# Revit family: TESK_Насос вертикальный_SVM(T)-32
name_source: partatom
category: Оборудование
units: mm (PartAtom-declared; Revit-internal decimal feet)

## family parameters
Всегда вертикально = Да
Классификация = Насос
На основе рабочей плоскости = Нет
Общий = Нет
При загрузке вырезать с полостями = Нет
Размер круглого соединителя = Использовать диаметр
Тип детали = Вставляется
Точка расчета площади = Нет

## types (64) — shared parameters
ADSK_Версия Revit = 2019
ADSK_Версия семейства = 1.0
ADSK_Диаметр условный = 65 мм
ADSK_Единица измерения = шт.
ADSK_Завод-изготовитель = TESK
ADSK_Классификация нагрузок = Прочее
ADSK_Количество = 1
ADSK_Количество фаз = 3
ADSK_Количество фаз числовое = 3
ADSK_Коэффициент мощности = 1
ADSK_Наименование краткое = Вертикальный многоступенчатый центробежный насос
ADSK_Напряжение = 400 В
URL = www.teskpump.ru
Материал_1 = TESK_Черный_Условный
Материал_2 = TESK_Нержавеющая сталь
Материал_КорпусДвигателя = TESK_Черный_Ребра_Условный
Таблица_Поиска = TESK_SVM(T)-32
УГО_Длина = 320 мм
Фланец_Толщина = 24 мм

## per-type parameters (varying)
| type | ADSK_Код изделия | ADSK_Масса | ADSK_Масса_Текст | ADSK_Наименование | ADSK_Номинальная мощность | ADSK_Полная мощность | D_Башня | Высота_Башня | Высота_Корпуса | Двигатель_Высота | Двигатель_ОтступКоробки | Двигатель_Ширина | Материал_КорпусУлитка | Напор максимальный | Толщина_ФланцаДвигателя |
| SVM 32-10-1 1.5kW 3x380V 50Hz IE3 | 7732-10-10003380NSSF | 67 | 67 | Вертикальный многоступенчатый центробежный насос SVM, DN65, PN25-40, Hmax=14м (3x380V 50Hz IE3) | 2 кВт | 2 кВ·А | 143 мм | 180 мм | 505 мм | 333 мм | 155 мм | 190 мм | TESK_Нержавеющая сталь | 14 | 10 мм |
| SVM 32-1 2.2kW 3x380V 50Hz IE3 | 7732-10003380NSSF | 67 | 67 | Вертикальный многоступенчатый центробежный насос SVM, DN65, PN25-40, Hmax=18м (3x380V 50Hz IE3) | 2 кВт | 2 кВ·А | 143 мм | 180 мм | 505 мм | 333 мм | 155 мм | 190 мм | TESK_Нержавеющая сталь | 18 | 10 мм |
| SVM 32-20-2 3kW 3x380V 50Hz IE3 | 7732-2-20003380NSSF | 83 | 83 | Вертикальный многоступенчатый центробежный насос SVM, DN65, PN25-40, Hmax=29м (3x380V 50Hz IE3) | 3 кВт | 3 кВ·А | 173 мм | 200 мм | 575 мм | 370 мм | 185 мм | 230 мм | TESK_Нержавеющая сталь | 29 | 11 мм |
| SVM 32-2 4kW 3x380V 50Hz IE3 | 7732-20003380NSSF | 83 | 83 | Вертикальный многоступенчатый центробежный насос SVM, DN65, PN25-40, Hmax=36м (3x380V 50Hz IE3) | 4 кВт | 4 кВ·А | 173 мм | 200 мм | 575 мм | 370 мм | 185 мм | 230 мм | TESK_Нержавеющая сталь | 36 | 11 мм |
| SVM 32-30-2 5.5kW 3x380V 50Hz IE3 | 7732-32003380NSSF | 100 | 100 | Вертикальный многоступенчатый центробежный насос SVM, DN65, PN25-40, Hmax=47м (3x380V 50Hz IE3) | 6 кВт | 6 кВ·А | 195 мм | 220 мм | 645 мм | 435 мм | 208 мм | 260 мм | TESK_Нержавеющая сталь | 47 | 13 мм |
| SVM 32-3 5.5kW 3x380V 50Hz IE3 | 7732-30003380NSSF | 100 | 100 | Вертикальный многоступенчатый центробежный насос SVM, DN65, PN25-40, Hmax=54м (3x380V 50Hz IE3) | 6 кВт | 6 кВ·А | 195 мм | 220 мм | 645 мм | 435 мм | 208 мм | 260 мм | TESK_Нержавеющая сталь | 54 | 13 мм |
| SVM 32-40-2 7.5kW 3x380V 50Hz IE3 | 7732-40-2003380NSSF | 109 | 109 | Вертикальный многоступенчатый центробежный насос SVM, DN65, PN25-40, Hmax=65м (3x380V 50Hz IE3) | 8 кВт | 8 кВ·А | 195 мм | 240 мм | 715 мм | 435 мм | 208 мм | 260 мм | TESK_Нержавеющая сталь | 65 | 13 мм |
| SVM 32-4 7.5kW 3x380V 50Hz IE3 | 7732-40003380NSSF | 109 | 109 | Вертикальный многоступенчатый центробежный насос SVM, DN65, PN25-40, Hmax=72м (3x380V 50Hz IE3) | 8 кВт | 8 кВ·А | 195 мм | 240 мм | 715 мм | 435 мм | 208 мм | 260 мм | TESK_Нержавеющая сталь | 72 | 13 мм |
| SVM 32-50-2 11kW 3x380V 50Hz IE3 | 7732-5-20003380NSSF | 181 | 181 | Вертикальный многоступенчатый центробежный насос SVM, DN65, PN25-40, Hmax=83м (3x380V 50Hz IE3) | 11 кВт | 11 кВ·А | 263 мм | 260 мм | 890 мм | 580 мм | 260 мм | 350 мм | TESK_Нержавеющая сталь | 83 | 17 мм |
| SVM 32-5 11kW 3x380V 50Hz IE3 | 7732-50003380NSSF | 181 | 181 | Вертикальный многоступенчатый центробежный насос SVM, DN65, PN25-40, Hmax=90м (3x380V 50Hz IE3) | 11 кВт | 11 кВ·А | 263 мм | 260 мм | 890 мм | 580 мм | 260 мм | 350 мм | TESK_Нержавеющая сталь | 90 | 17 мм |
| SVM 32-60-2 11kW 3x380V 50Hz IE3 | 7732-6-20003380NSSF | 185 | 185 | Вертикальный многоступенчатый центробежный насос SVM, DN65, PN25-40, Hmax=101м (3x380V 50Hz IE3) | 11 кВт | 11 кВ·А | 263 мм | 280 мм | 960 мм | 580 мм | 260 мм | 350 мм | TESK_Нержавеющая сталь | 101 | 17 мм |
| SVM 32-6 11kW 3x380V 50Hz IE3 | 7732-60003380NSSF | 185 | 185 | Вертикальный многоступенчатый центробежный насос SVM, DN65, PN25-40, Hmax=108м (3x380V 50Hz IE3) | 11 кВт | 11 кВ·А | 263 мм | 280 мм | 960 мм | 580 мм | 260 мм | 350 мм | TESK_Нержавеющая сталь | 108 | 17 мм |
| SVM 32-70-2 15kW 3x380V 50Hz IE3 | 7732-7-20003380NSSF | 199 | 199 | Вертикальный многоступенчатый центробежный насос SVM, DN65, PN25-40, Hmax=119м (3x380V 50Hz IE3) | 15 кВт | 15 кВ·А | 263 мм | 300 мм | 1030 мм | 580 мм | 260 мм | 350 мм | TESK_Нержавеющая сталь | 119 | 17 мм |
| SVM 32-7 15kW 3x380V 50Hz IE3 | 7732-70003380NSSF | 199 | 199 | Вертикальный многоступенчатый центробежный насос SVM, DN65, PN25-40, Hmax=126м (3x380V 50Hz IE3) | 15 кВт | 15 кВ·А | 263 мм | 300 мм | 1030 мм | 580 мм | 260 мм | 350 мм | TESK_Нержавеющая сталь | 126 | 17 мм |
| SVM 32-80-2 15kW 3x380V 50Hz IE3 | 7732-8-20003380NSSF | 203 | 203 | Вертикальный многоступенчатый центробежный насос SVM, DN65, PN25-40, Hmax=136м (3x380V 50Hz IE3) | 15 кВт | 15 кВ·А | 263 мм | 320 мм | 1100 мм | 580 мм | 260 мм | 350 мм | TESK_Нержавеющая сталь | 136 | 17 мм |
| SVM 32-8 15kW 3x380V 50Hz IE3 | 7732-80003380NSSF | 203 | 203 | Вертикальный многоступенчатый центробежный насос SVM, DN65, PN25-40, Hmax=144м (3x380V 50Hz IE3) | 15 кВт | 15 кВ·А | 263 мм | 320 мм | 1100 мм | 580 мм | 260 мм | 350 мм | TESK_Нержавеющая сталь | 144 | 17 мм |
| SVM 32-90-2 18.5kW 3x380V 50Hz IE3 | 7732-9-20003380NSSF | 222 | 222 | Вертикальный многоступенчатый центробежный насос SVM, DN65, PN25-40, Hmax=154м (3x380V 50Hz IE3) | 19 кВт | 19 кВ·А | 263 мм | 340 мм | 1170 мм | 610 мм | 260 мм | 350 мм | TESK_Нержавеющая сталь | 154 | 18 мм |
| SVM 32-9 18.5kW 3x380V 50Hz IE3 | 7732-90003380NSSF | 222 | 222 | Вертикальный многоступенчатый центробежный насос SVM, DN65, PN25-40, Hmax=162м (3x380V 50Hz IE3) | 19 кВт | 19 кВ·А | 263 мм | 340 мм | 1170 мм | 610 мм | 260 мм | 350 мм | TESK_Нержавеющая сталь | 162 | 18 мм |
| SVM 32-100-2 18.5kW 3x380V 50Hz IE3 | 7732-1020003380NSSF | 227 | 227 | Вертикальный многоступенчатый центробежный насос SVM, DN65, PN25-40, Hmax=175м (3x380V 50Hz IE3) | 19 кВт | 19 кВ·А | 263 мм | 360 мм | 1240 мм | 610 мм | 260 мм | 350 мм | TESK_Нержавеющая сталь | 175 | 18 мм |
| SVM 32-10 18.5kW 3x380V 50Hz IE3 | 7732-1000003380NSSF | 227 | 227 | Вертикальный многоступенчатый центробежный насос SVM, DN65, PN25-40, Hmax=182м (3x380V 50Hz IE3) | 19 кВт | 19 кВ·А | 263 мм | 360 мм | 1240 мм | 610 мм | 260 мм | 350 мм | TESK_Нержавеющая сталь | 182 | 18 мм |
| SVM 32-110-2 22kW 3x380V 50Hz IE3 | 7732-110003380N-2SSF | 272 | 272 | Вертикальный многоступенчатый центробежный насос SVM, DN65, PN25-40, Hmax=193м (3x380V 50Hz IE3) | 22 кВт | 22 кВ·А | 270 мм | 380 мм | 1310 мм | 645 мм | 285 мм | 360 мм | TESK_Нержавеющая сталь | 193 | 19 мм |
| SVM 32-11 22kW 3x380V 50Hz IE3 | 7732-110003380NSSF | 272 | 272 | Вертикальный многоступенчатый центробежный насос SVM, DN65, PN25-40, Hmax=200м (3x380V 50Hz IE3) | 22 кВт | 22 кВ·А | 270 мм | 380 мм | 1310 мм | 645 мм | 285 мм | 360 мм | TESK_Нержавеющая сталь | 200 | 19 мм |
| SVM 32-120-2 22kW 3x380V 50Hz IE3 | 7732-12-20003380NSSF | 276 | 276 | Вертикальный многоступенчатый центробежный насос SVM, DN65, PN25-40, Hmax=211м (3x380V 50Hz IE3) | 22 кВт | 22 кВ·А | 270 мм | 400 мм | 1380 мм | 645 мм | 285 мм | 360 мм | TESK_Нержавеющая сталь | 211 | 19 мм |
| SVM 32-12 22kW 3x380V 50Hz IE3 | 7732-120003380NSSF | 276 | 276 | Вертикальный многоступенчатый центробежный насос SVM, DN65, PN25-40, Hmax=218м (3x380V 50Hz IE3) | 22 кВт | 22 кВ·А | 270 мм | 400 мм | 1380 мм | 645 мм | 285 мм | 360 мм | TESK_Нержавеющая сталь | 218 | 19 мм |
| SVM 32-130-2 30kW 3x380V 50Hz IE3 | 7732-1320003380NSSF | 337 | 337 | Вертикальный многоступенчатый центробежный насос SVM, DN65, PN25-40, Hmax=230м (3x380V 50Hz IE3) | 30 кВт | 30 кВ·А | 300 мм | 420 мм | 1450 мм | 705 мм | 310 мм | 400 мм | TESK_Нержавеющая сталь | 230 | 21 мм |
| SVM 32-13 30kW 3x380V 50Hz IE3 | 7732-130003380NSSF | 337 | 337 | Вертикальный многоступенчатый центробежный насос SVM, DN65, PN25-40, Hmax=237м (3x380V 50Hz IE3) | 30 кВт | 30 кВ·А | 300 мм | 420 мм | 1450 мм | 705 мм | 310 мм | 400 мм | TESK_Нержавеющая сталь | 237 | 21 мм |
| SVM 32-140-2 30kW 3x380V 50Hz IE3 | 7732-1420003380NSSF | 341 | 341 | Вертикальный многоступенчатый центробежный насос SVM, DN65, PN25-40, Hmax=247м (3x380V 50Hz IE3) | 30 кВт | 30 кВ·А | 300 мм | 440 мм | 1520 мм | 705 мм | 310 мм | 400 мм | TESK_Нержавеющая сталь | 247 | 21 мм |
| SVM 32-14 30kW 3x380V 50Hz IE3 | 7732-140003380NSSF | 341 | 341 | Вертикальный многоступенчатый центробежный насос SVM, DN65, PN25-40, Hmax=255м (3x380V 50Hz IE3) | 30 кВт | 30 кВ·А | 300 мм | 440 мм | 1520 мм | 705 мм | 310 мм | 400 мм | TESK_Нержавеющая сталь | 255 | 21 мм |
| SVM 32-150-2 30kW 3x380V 50Hz IE3 | 7732-15-20003380NSSF | 345 | 345 | Вертикальный многоступенчатый центробежный насос SVM, DN65, PN25-40, Hmax=266м (3x380V 50Hz IE3) | 30 кВт | 30 кВ·А | 300 мм | 460 мм | 1590 мм | 705 мм | 310 мм | 400 мм | TESK_Нержавеющая сталь | 266 | 21 мм |
| SVM 32-15 30kW 3x380V 50Hz IE3 | 7732-150003380NSSF | 345 | 345 | Вертикальный многоступенчатый центробежный насос SVM, DN65, PN25-40, Hmax=274м (3x380V 50Hz IE3) | 30 кВт | 30 кВ·А | 300 мм | 460 мм | 1590 мм | 705 мм | 310 мм | 400 мм | TESK_Нержавеющая сталь | 274 | 21 мм |
| SVM 32-160-2 30kW 3x380V 50Hz IE3 | 7732-16-20003380NSSF | 350 | 350 | Вертикальный многоступенчатый центробежный насос SVM, DN65, PN25-40, Hmax=284м (3x380V 50Hz IE3) | 30 кВт | 30 кВ·А | 300 мм | 480 мм | 1660 мм | 705 мм | 310 мм | 400 мм | TESK_Нержавеющая сталь | 284 | 21 мм |
| SVM 32-16 30kW 3x380V 50Hz IE3 | 7732-160003380NSSF | 350 | 350 | Вертикальный многоступенчатый центробежный насос SVM, DN65, PN25-40, Hmax=292м (3x380V 50Hz IE3) | 30 кВт | 30 кВ·А | 300 мм | 480 мм | 1660 мм | 705 мм | 310 мм | 400 мм | TESK_Нержавеющая сталь | 292 | 21 мм |
| SVMT 32-10-1 1.5kW 3x380V 50Hz IE3 | 7732-10-10003380N | 67 | 67 | Вертикальный многоступенчатый центробежный насос SVMT, DN65, PN25-40, Hmax=14м (3x380V 50Hz IE3) | 2 кВт | 2 кВ·А | 143 мм | 180 мм | 505 мм | 333 мм | 155 мм | 190 мм | TESK_Черный_Условный | 14 | 10 мм |
| SVMT 32-1 2.2kW 3x380V 50Hz IE3 | 7732-10003380N | 67 | 67 | Вертикальный многоступенчатый центробежный насос SVMT, DN65, PN25-40, Hmax=18м (3x380V 50Hz IE3) | 2 кВт | 2 кВ·А | 143 мм | 180 мм | 505 мм | 333 мм | 155 мм | 190 мм | TESK_Черный_Условный | 18 | 10 мм |
| SVMT 32-20-2 3kW 3x380V 50Hz IE3 | 7732-2-20003380N | 83 | 83 | Вертикальный многоступенчатый центробежный насос SVMT, DN65, PN25-40, Hmax=29м (3x380V 50Hz IE3) | 3 кВт | 3 кВ·А | 173 мм | 200 мм | 575 мм | 370 мм | 185 мм | 230 мм | TESK_Черный_Условный | 29 | 11 мм |
| SVMT 32-2 4kW 3x380V 50Hz IE3 | 7732-20003380N | 83 | 83 | Вертикальный многоступенчатый центробежный насос SVMT, DN65, PN25-40, Hmax=36м (3x380V 50Hz IE3) | 4 кВт | 4 кВ·А | 173 мм | 200 мм | 575 мм | 370 мм | 185 мм | 230 мм | TESK_Черный_Условный | 36 | 11 мм |
| SVMT 32-30-2 5.5kW 3x380V 50Hz IE3 | 7732-32003380N | 100 | 100 | Вертикальный многоступенчатый центробежный насос SVMT, DN65, PN25-40, Hmax=47м (3x380V 50Hz IE3) | 6 кВт | 6 кВ·А | 195 мм | 220 мм | 645 мм | 435 мм | 208 мм | 260 мм | TESK_Черный_Условный | 47 | 13 мм |
| SVMT 32-3 5.5kW 3x380V 50Hz IE3 | 7732-30003380N | 100 | 100 | Вертикальный многоступенчатый центробежный насос SVMT, DN65, PN25-40, Hmax=54м (3x380V 50Hz IE3) | 6 кВт | 6 кВ·А | 195 мм | 220 мм | 645 мм | 435 мм | 208 мм | 260 мм | TESK_Черный_Условный | 54 | 13 мм |
| SVMT 32-40-2 7.5kW 3x380V 50Hz IE3 | 7732-420003380N | 109 | 109 | Вертикальный многоступенчатый центробежный насос SVMT, DN65, PN25-40, Hmax=65м (3x380V 50Hz IE3) | 8 кВт | 8 кВ·А | 195 мм | 240 мм | 715 мм | 435 мм | 208 мм | 260 мм | TESK_Черный_Условный | 65 | 13 мм |
| SVMT 32-4 7.5kW 3x380V 50Hz IE3 | 7732-40003380N | 109 | 109 | Вертикальный многоступенчатый центробежный насос SVMT, DN65, PN25-40, Hmax=72м (3x380V 50Hz IE3) | 8 кВт | 8 кВ·А | 195 мм | 240 мм | 715 мм | 435 мм | 208 мм | 260 мм | TESK_Черный_Условный | 72 | 13 мм |
| SVMT 32-50-2 11kW 3x380V 50Hz IE3 | 7732-5-20003380N | 181 | 181 | Вертикальный многоступенчатый центробежный насос SVMT, DN65, PN25-40, Hmax=83м (3x380V 50Hz IE3) | 11 кВт | 11 кВ·А | 263 мм | 260 мм | 890 мм | 580 мм | 260 мм | 350 мм | TESK_Черный_Условный | 83 | 17 мм |
| SVMT 32-5 11kW 3x380V 50Hz IE3 | 7732-50003380N | 181 | 181 | Вертикальный многоступенчатый центробежный насос SVMT, DN65, PN25-40, Hmax=90м (3x380V 50Hz IE3) | 11 кВт | 11 кВ·А | 263 мм | 260 мм | 890 мм | 580 мм | 260 мм | 350 мм | TESK_Черный_Условный | 90 | 17 мм |
| SVMT 32-60-2 11kW 3x380V 50Hz IE3 | 7732-6-20003380N | 185 | 185 | Вертикальный многоступенчатый центробежный насос SVMT, DN65, PN25-40, Hmax=101м (3x380V 50Hz IE3) | 11 кВт | 11 кВ·А | 263 мм | 280 мм | 960 мм | 580 мм | 260 мм | 350 мм | TESK_Черный_Условный | 101 | 17 мм |
| SVMT 32-6 11kW 3x380V 50Hz IE3 | 7732-60003380N | 185 | 185 | Вертикальный многоступенчатый центробежный насос SVMT, DN65, PN25-40, Hmax=108м (3x380V 50Hz IE3) | 11 кВт | 11 кВ·А | 263 мм | 280 мм | 960 мм | 580 мм | 260 мм | 350 мм | TESK_Черный_Условный | 108 | 17 мм |
| SVMT 32-70-2 15kW 3x380V 50Hz IE3 | 7732-7-20003380N | 199 | 199 | Вертикальный многоступенчатый центробежный насос SVMT, DN65, PN25-40, Hmax=119м (3x380V 50Hz IE3) | 15 кВт | 15 кВ·А | 263 мм | 300 мм | 1030 мм | 580 мм | 260 мм | 350 мм | TESK_Черный_Условный | 119 | 17 мм |
| SVMT 32-7 15kW 3x380V 50Hz IE3 | 7732-70003380N | 199 | 199 | Вертикальный многоступенчатый центробежный насос SVMT, DN65, PN25-40, Hmax=126м (3x380V 50Hz IE3) | 15 кВт | 15 кВ·А | 263 мм | 300 мм | 1030 мм | 580 мм | 260 мм | 350 мм | TESK_Черный_Условный | 126 | 17 мм |
| SVMT 32-80-2 15kW 3x380V 50Hz IE3 | 7732-8-20003380N | 203 | 203 | Вертикальный многоступенчатый центробежный насос SVMT, DN65, PN25-40, Hmax=136м (3x380V 50Hz IE3) | 15 кВт | 15 кВ·А | 263 мм | 320 мм | 1100 мм | 580 мм | 260 мм | 350 мм | TESK_Черный_Условный | 136 | 17 мм |
| SVMT 32-8 15kW 3x380V 50Hz IE3 | 7732-80003380N | 203 | 203 | Вертикальный многоступенчатый центробежный насос SVMT, DN65, PN25-40, Hmax=144м (3x380V 50Hz IE3) | 15 кВт | 15 кВ·А | 263 мм | 320 мм | 1100 мм | 580 мм | 260 мм | 350 мм | TESK_Черный_Условный | 144 | 17 мм |
| SVMT 32-90-2 18.5kW 3x380V 50Hz IE3 | 7732-9-20003380N | 222 | 222 | Вертикальный многоступенчатый центробежный насос SVMT, DN65, PN25-40, Hmax=154м (3x380V 50Hz IE3) | 19 кВт | 19 кВ·А | 263 мм | 340 мм | 1170 мм | 610 мм | 260 мм | 350 мм | TESK_Черный_Условный | 154 | 18 мм |
| SVMT 32-9 18.5kW 3x380V 50Hz IE3 | 7732-90003380N | 222 | 222 | Вертикальный многоступенчатый центробежный насос SVMT, DN65, PN25-40, Hmax=162м (3x380V 50Hz IE3) | 19 кВт | 19 кВ·А | 263 мм | 340 мм | 1170 мм | 610 мм | 260 мм | 350 мм | TESK_Черный_Условный | 162 | 18 мм |
| SVMT 32-100-2 18.5kW 3x380V 50Hz IE3 | 7732-1020003380N | 227 | 227 | Вертикальный многоступенчатый центробежный насос SVMT, DN65, PN25-40, Hmax=175м (3x380V 50Hz IE3) | 19 кВт | 19 кВ·А | 263 мм | 360 мм | 1240 мм | 610 мм | 260 мм | 350 мм | TESK_Черный_Условный | 175 | 18 мм |
| SVMT 32-10 18.5kW 3x380V 50Hz IE3 | 7732-1000003380N | 227 | 227 | Вертикальный многоступенчатый центробежный насос SVMT, DN65, PN25-40, Hmax=182м (3x380V 50Hz IE3) | 19 кВт | 19 кВ·А | 263 мм | 360 мм | 1240 мм | 610 мм | 260 мм | 350 мм | TESK_Черный_Условный | 182 | 18 мм |
| SVMT 32-110-2 22kW 3x380V 50Hz IE3 | 7732-110003380N-2 | 272 | 272 | Вертикальный многоступенчатый центробежный насос SVMT, DN65, PN25-40, Hmax=193м (3x380V 50Hz IE3) | 22 кВт | 22 кВ·А | 270 мм | 380 мм | 1310 мм | 645 мм | 285 мм | 360 мм | TESK_Черный_Условный | 193 | 19 мм |
| SVMT 32-11 22kW 3x380V 50Hz IE3 | 7732-110003380N | 272 | 272 | Вертикальный многоступенчатый центробежный насос SVMT, DN65, PN25-40, Hmax=200м (3x380V 50Hz IE3) | 22 кВт | 22 кВ·А | 270 мм | 380 мм | 1310 мм | 645 мм | 285 мм | 360 мм | TESK_Черный_Условный | 200 | 19 мм |
| SVMT 32-120-2 22kW 3x380V 50Hz IE3 | 7732-12-20003380N | 276 | 276 | Вертикальный многоступенчатый центробежный насос SVMT, DN65, PN25-40, Hmax=211м (3x380V 50Hz IE3) | 22 кВт | 22 кВ·А | 270 мм | 400 мм | 1380 мм | 645 мм | 285 мм | 360 мм | TESK_Черный_Условный | 211 | 19 мм |
| SVMT 32-12 22kW 3x380V 50Hz IE3 | 7732-120003380N | 276 | 276 | Вертикальный многоступенчатый центробежный насос SVMT, DN65, PN25-40, Hmax=218м (3x380V 50Hz IE3) | 22 кВт | 22 кВ·А | 270 мм | 400 мм | 1380 мм | 645 мм | 285 мм | 360 мм | TESK_Черный_Условный | 218 | 19 мм |
| SVMT 32-130-2 30kW 3x380V 50Hz IE3 | 7732-1320003380N | 337 | 337 | Вертикальный многоступенчатый центробежный насос SVMT, DN65, PN25-40, Hmax=230м (3x380V 50Hz IE3) | 30 кВт | 30 кВ·А | 300 мм | 420 мм | 1450 мм | 705 мм | 310 мм | 400 мм | TESK_Черный_Условный | 230 | 21 мм |
| SVMT 32-13 30kW 3x380V 50Hz IE3 | 7732-130003380N | 337 | 337 | Вертикальный многоступенчатый центробежный насос SVMT, DN65, PN25-40, Hmax=237м (3x380V 50Hz IE3) | 30 кВт | 30 кВ·А | 300 мм | 420 мм | 1450 мм | 705 мм | 310 мм | 400 мм | TESK_Черный_Условный | 237 | 21 мм |
| SVMT 32-140-2 30kW 3x380V 50Hz IE3 | 7732-1420003380N | 341 | 341 | Вертикальный многоступенчатый центробежный насос SVMT, DN65, PN25-40, Hmax=247м (3x380V 50Hz IE3) | 30 кВт | 30 кВ·А | 300 мм | 440 мм | 1520 мм | 705 мм | 310 мм | 400 мм | TESK_Черный_Условный | 247 | 21 мм |
| SVMT 32-14 30kW 3x380V 50Hz IE3 | 7732-140003380N | 341 | 341 | Вертикальный многоступенчатый центробежный насос SVMT, DN65, PN25-40, Hmax=255м (3x380V 50Hz IE3) | 30 кВт | 30 кВ·А | 300 мм | 440 мм | 1520 мм | 705 мм | 310 мм | 400 мм | TESK_Черный_Условный | 255 | 21 мм |
| SVMT 32-150-2 30kW 3x380V 50Hz IE3 | 7732-15-20003380N | 345 | 345 | Вертикальный многоступенчатый центробежный насос SVMT, DN65, PN25-40, Hmax=266м (3x380V 50Hz IE3) | 30 кВт | 30 кВ·А | 300 мм | 460 мм | 1590 мм | 705 мм | 310 мм | 400 мм | TESK_Черный_Условный | 266 | 21 мм |
| SVMT 32-15 30kW 3x380V 50Hz IE3 | 7732-150003380N | 345 | 345 | Вертикальный многоступенчатый центробежный насос SVMT, DN65, PN25-40, Hmax=274м (3x380V 50Hz IE3) | 30 кВт | 30 кВ·А | 300 мм | 460 мм | 1590 мм | 705 мм | 310 мм | 400 мм | TESK_Черный_Условный | 274 | 21 мм |
| SVMT 32-160-2 30kW 3x380V 50Hz IE3 | 7732-16-20003380N | 350 | 350 | Вертикальный многоступенчатый центробежный насос SVMT, DN65, PN25-40, Hmax=284м (3x380V 50Hz IE3) | 30 кВт | 30 кВ·А | 300 мм | 480 мм | 1660 мм | 705 мм | 310 мм | 400 мм | TESK_Черный_Условный | 284 | 21 мм |
| SVMT 32-16 30kW 3x380V 50Hz IE3 | 7732-160003380N | 350 | 350 | Вертикальный многоступенчатый центробежный насос SVMT, DN65, PN25-40, Hmax=292м (3x380V 50Hz IE3) | 30 кВт | 30 кВ·А | 300 мм | 480 мм | 1660 мм | 705 мм | 310 мм | 400 мм | TESK_Черный_Условный | 292 | 21 мм |

note: column(s) folded — value = type name in every type: ADSK_Марка
